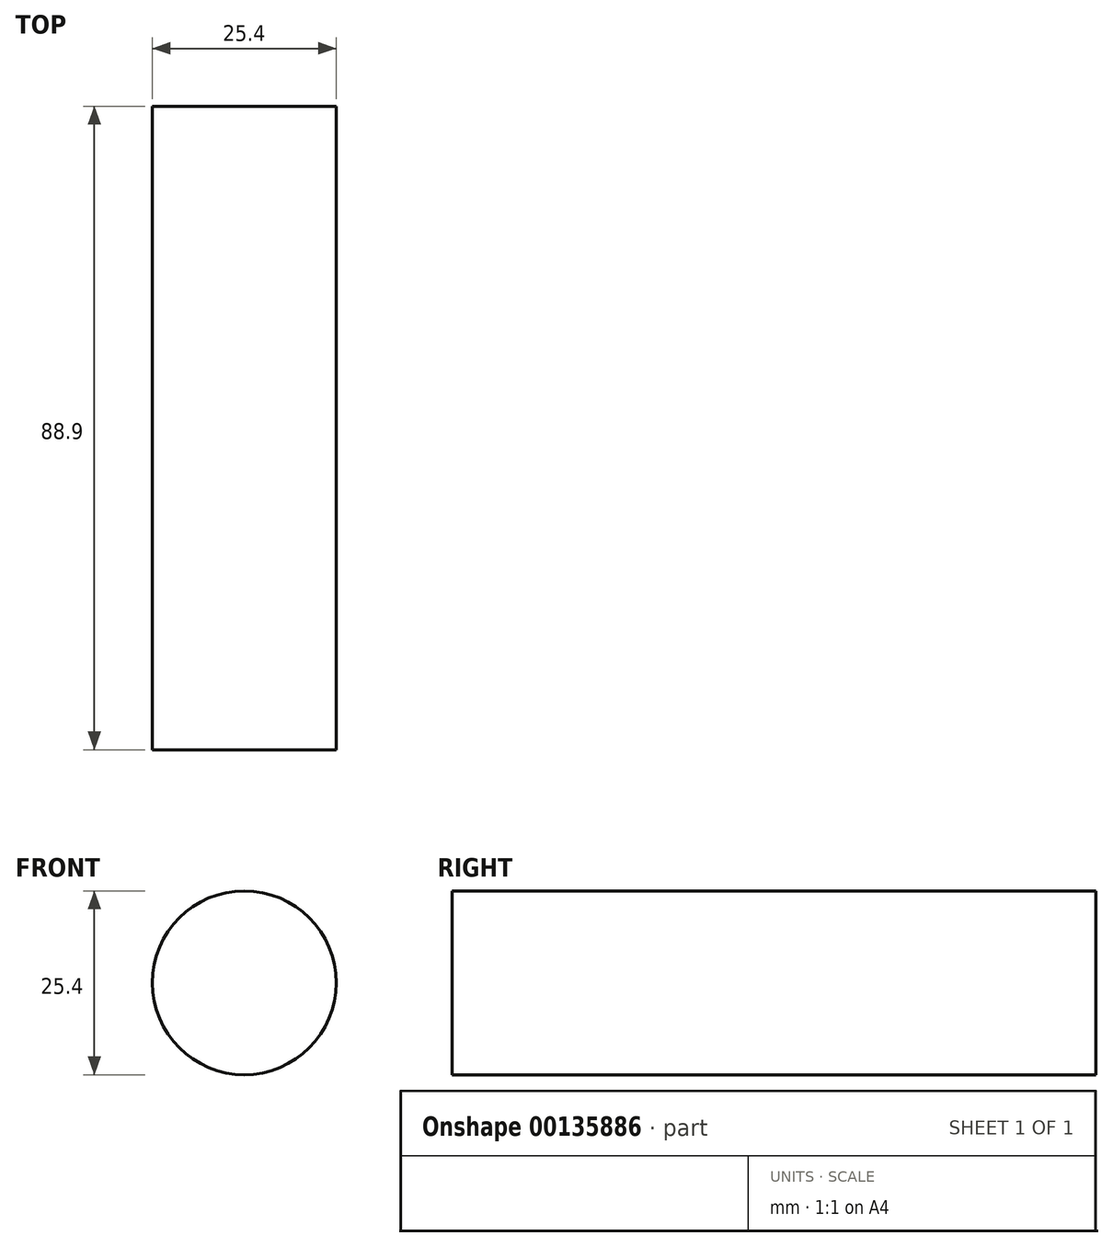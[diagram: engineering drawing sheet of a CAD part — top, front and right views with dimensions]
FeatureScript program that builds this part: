
annotation { "Feature Type Name" : "Feature", "Feature Type Description" : "" }
export const myFeature = defineFeature(function(context is Context, id is Id, definition is map)
    precondition{}
    {
        {
            var Q0;
            Q0=qCreatedBy(makeId("Front.planeOp"),FACE);
            var sketch = newSketch(context, id + "F0", { "sketchPlane" : qUnion([Q0])});
            skCircle(sketch, "E0", {"center": v(0, 0) * mm, "radius": 12.7 * mm});
            skSolve(sketch);
        }
        {
            var Q0;
            Q0=makeQuery(id+"F0.imprint","IMPRINT",FACE,{"disambiguationData":[TD([[makeQuery(id+"F0.imprint","IMPRINT",EDGE,{"derivedFrom":sQuery(id+"F0.wireOp",EDGE,"E0")}),1.0]])]});
            extrude(context, id + "F1", {"entities" : qUnion([Q0]), "oppositeDirection" : true, "depth" : 88.9 * mm});
        }
    });
